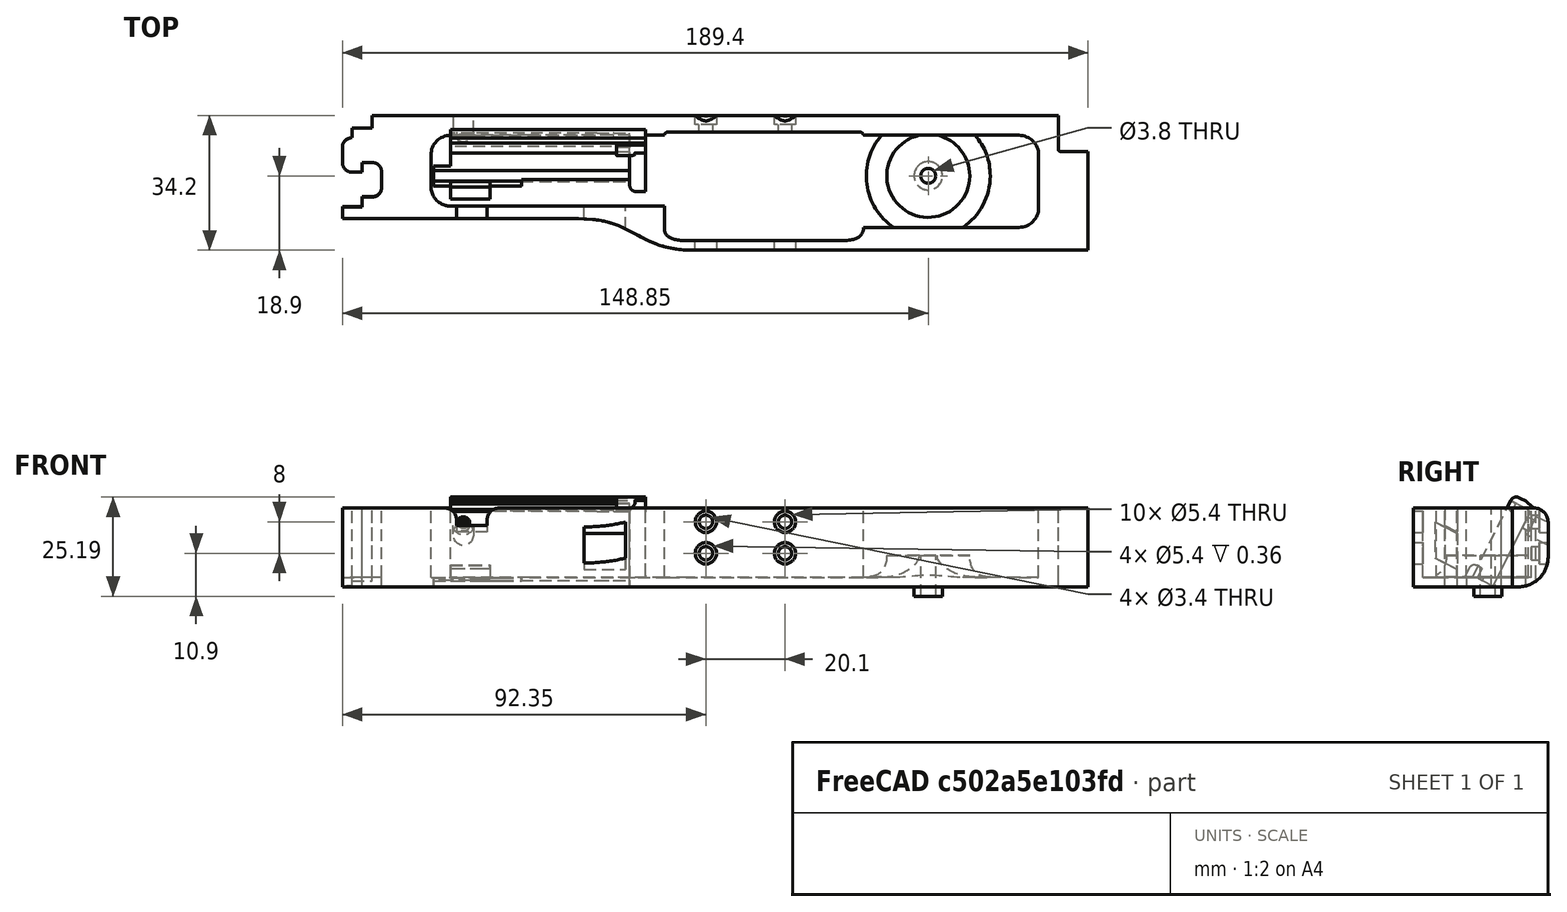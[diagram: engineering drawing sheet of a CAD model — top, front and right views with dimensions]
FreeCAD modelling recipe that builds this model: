
FCSTD DOCUMENT  (FreeCAD 0.19R0.19.2)
Label: v0_99
License: All rights reserved
LicenseURL: http://en.wikipedia.org/wiki/All_rights_reserved
objects: Sketcher::SketchObject×34, Part::Extrusion×28, Part::Cut×14, Part::Fillet×13, Part::MultiFuse×10, Part::Box×8, App::MeasureDistance×4, Part::Revolution×1, Mesh::Feature×1
note: 108 computed .brp shape members not serialized (recipe doc carries the construction recipe); baked Part::Feature solids carry a one-line shape summary decoded from their .brp

FEATURE [Sketcher::SketchObject] Sketch
  FullyConstrained = true
  sketch-geometry (36):
    g0: LineSegment StartX=0 StartY=0 StartZ=0 EndX=154.4 EndY=0 EndZ=0
    g1: LineSegment StartX=154.4 StartY=0 StartZ=0 EndX=154.4 EndY=-7.6 EndZ=0
    g2: LineSegment StartX=32.5209 StartY=-26.2 StartZ=0 EndX=-7.5 EndY=-26.2 EndZ=0
    g3: LineSegment StartX=61.85 StartY=-34.2 StartZ=0 EndX=161.9 EndY=-34.2 EndZ=0
    g4-g8: Circle x5 (B-spline internal-alignment scaffolding for g9; pole/knot coordinates omitted)
    g9: BSplineCurve PolesCount=5 KnotsCount=3 Degree=3 IsPeriodic=0
    g10: GeomPoint X=61.85 Y=-34.2 Z=0
    g11: GeomPoint X=47.185 Y=-30.2 Z=0
    g12: GeomPoint X=32.5209 Y=-26.2 Z=0
    g13: Circle CenterX=121.35 CenterY=-14.3 CenterZ=0 NormalX=0 NormalY=0 NormalZ=1 AngleXU=0 Radius=3.25
    g14: LineSegment StartX=-7.5 StartY=-26.2 StartZ=0 EndX=-27.5 EndY=-26.2 EndZ=0
    g15: LineSegment StartX=-20 StartY=0 StartZ=0 EndX=0 EndY=0 EndZ=0
    g16: LineSegment StartX=-25 StartY=-3.1 StartZ=0 EndX=-20 EndY=-3.1 EndZ=0
    g17: LineSegment StartX=-25 StartY=-3.1 StartZ=0 EndX=-25 EndY=-5.6 EndZ=0
    g18: LineSegment StartX=-27.5 StartY=-8.1 StartZ=0 EndX=-27.5 EndY=-11.85 EndZ=0
    g19: ArcOfCircle CenterX=-25 CenterY=-8.1 CenterZ=0 NormalX=0 NormalY=0 NormalZ=1 AngleXU=0 Radius=2.5 StartAngle=1.5708 EndAngle=3.14159
    g20: LineSegment StartX=-25 StartY=-14.35 StartZ=0 EndX=-22.5 EndY=-14.35 EndZ=0
    g21: ArcOfCircle CenterX=-25 CenterY=-11.85 CenterZ=0 NormalX=0 NormalY=0 NormalZ=1 AngleXU=0 Radius=2.5 StartAngle=3.14159 EndAngle=4.71239
    g22: LineSegment StartX=-22.5 StartY=-14.35 StartZ=0 EndX=-22.5 EndY=-11.85 EndZ=0
    g23: LineSegment StartX=-22.5 StartY=-11.85 StartZ=0 EndX=-20 EndY=-11.85 EndZ=0
    g24: ArcOfCircle CenterX=-20 CenterY=-14.35 CenterZ=0 NormalX=0 NormalY=0 NormalZ=1 AngleXU=0 Radius=2.5 StartAngle=8e-16 EndAngle=1.5708
    g25: LineSegment StartX=-17.5 StartY=-14.35 StartZ=0 EndX=-17.5 EndY=-18.1 EndZ=0
    g26: ArcOfCircle CenterX=-20 CenterY=-18.1 CenterZ=0 NormalX=0 NormalY=0 NormalZ=1 AngleXU=0 Radius=2.5 StartAngle=4.71239 EndAngle=6.28319
    g27: LineSegment StartX=-22.5 StartY=-20.6 StartZ=0 EndX=-20 EndY=-20.6 EndZ=0
    g28: LineSegment StartX=-22.5 StartY=-20.6 StartZ=0 EndX=-22.5 EndY=-23.1 EndZ=0
    g29: LineSegment StartX=-27.5 StartY=-23.1 StartZ=0 EndX=-22.5 EndY=-23.1 EndZ=0
    g30: LineSegment StartX=-20 StartY=-3.1 StartZ=0 EndX=-20 EndY=0 EndZ=0
    g31: LineSegment StartX=-27.5 StartY=-23.1 StartZ=0 EndX=-27.5 EndY=-26.2 EndZ=0
    g32: LineSegment StartX=154.4 StartY=-7.6 StartZ=0 EndX=154.4 EndY=-8.6 EndZ=0
    g33: ArcOfCircle CenterX=154.9 CenterY=-8.6 CenterZ=0 NormalX=0 NormalY=0 NormalZ=1 AngleXU=0 Radius=0.5 StartAngle=3.14159 EndAngle=4.71239
    g34: LineSegment StartX=154.9 StartY=-9.1 StartZ=0 EndX=161.9 EndY=-9.1 EndZ=0
    g35: LineSegment StartX=161.9 StartY=-34.2 StartZ=0 EndX=161.9 EndY=-9.1 EndZ=0
  constraints (72):
    c: PointOnObject(g0,g-2)
    c: Horizontal(g0)
    c: Distance(g0) = 154.4
    c: DistanceY(g-1,g0) = 0
    c: Vertical(g1)
    c: Distance(g1) = 7.6
    c: Coincident(g1,g0)
    c: Horizontal(g3)
    c: Horizontal(g2)
    c: Block(g2)
    c: Block(g3)
    c: Coincident(g9,g3)
    c: Weight(g4) = 1
    c: Equal(g4, g5-g8) x4
    c: Coincident(g9,g2)
    c: InternalAlignment(g4-g8 -> g9) x5
    c: InternalAlignment(g10,g9)
    c: InternalAlignment(g11,g9)
    c: InternalAlignment(g12,g9)
    c: Block(g9)
    c: Block(g13)
    c: Coincident(g14,g2)
    c: Horizontal(g14)
    c: Distance(g14) = 20
    c: Horizontal(g15)
    c: Distance(g15) = 20
    c: Coincident(g15,g0)
    c: Horizontal(g16)
    c: Vertical(g17)
    c: Coincident(g17,g16)
    c: Vertical(g18)
    c: Coincident(g19,g17)
    c: Block(g19)
    c: Coincident(g18,g19)
    c: Horizontal(g20)
    c: Coincident(g21,g18)
    c: Block(g21)
    c: Block(g20)
    c: Vertical(g22)
    c: Coincident(g22,g20)
    c: Horizontal(g23)
    c: Coincident(g23,g22)
    c: Coincident(g24,g23)
    c: Vertical(g25)
    c: Block(g24)
    c: Coincident(g25,g24)
    c: Coincident(g26,g25)
    c: Block(g26)
    c: Horizontal(g27)
    c: Coincident(g27,g26)
    c: Vertical(g28)
    c: Coincident(g28,g27)
    c: Horizontal(g29)
    c: Coincident(g29,g28)
    c: Block(g16)
    c: Block(g29)
    c: Coincident(g30,g16)
    c: Coincident(g30,g15)
    c: Vertical(g30)
    c: Coincident(g31,g29)
    c: Coincident(g31,g14)
    c: Vertical(g31)
    c: Vertical(g32)
    c: Distance(g32) = 1
    c: Coincident(g32,g1)
    c: Coincident(g33,g32)
    c: Block(g33)
    c: Coincident(g34,g33)
    c: Horizontal(g34)
    c: Coincident(g35,g3)
    c: Vertical(g35)
    c: Coincident(g34,g35)
FEATURE [Part::Extrusion] Extrude  label="mainBodyBaseExtrude"
  Base = -> Sketch
  Dir = (0,0,1)
  DirMode = 2
  FaceMakerClass = Part::FaceMakerBullseye
  LengthFwd = 2.4
  LengthRev = 0
  Solid = true
  Symmetric = false
FEATURE [Sketcher::SketchObject] Sketch001
  FullyConstrained = true
  sketch-geometry (59):
    g0: ArcOfCircle CenterX=144.4 CenterY=-10 CenterZ=0 NormalX=0 NormalY=0 NormalZ=1 AngleXU=0 Radius=5 StartAngle=4.345e-13 EndAngle=1.5708
    g1: LineSegment StartX=32.5209 StartY=-26.2 StartZ=0 EndX=-7.49911 EndY=-26.2 EndZ=0
    g2: LineSegment StartX=61.85 StartY=-34.2 StartZ=0 EndX=161.9 EndY=-34.2 EndZ=0
    g3: LineSegment StartX=0 StartY=0 StartZ=0 EndX=154.4 EndY=0 EndZ=0
    g4-g8: Circle x5 (B-spline internal-alignment scaffolding for g9; pole/knot coordinates omitted)
    g9: BSplineCurve PolesCount=5 KnotsCount=3 Degree=3 IsPeriodic=0
    g10: GeomPoint X=61.85 Y=-34.2 Z=0
    g11: GeomPoint X=47.1857 Y=-30.2 Z=0
    g12: GeomPoint X=32.5209 Y=-26.2 Z=0
    g13: LineSegment StartX=154.4 StartY=0 StartZ=0 EndX=154.4 EndY=-7.6 EndZ=0
    g14: LineSegment StartX=20 StartY=-5 StartZ=0 EndX=54.35 EndY=-5 EndZ=0
    g15: LineSegment StartX=104.85 StartY=-5 StartZ=0 EndX=144.4 EndY=-5 EndZ=0
    g16: LineSegment StartX=54.35 StartY=-23 StartZ=0 EndX=20 EndY=-23 EndZ=0
    g17: LineSegment StartX=-27.4991 StartY=-26.2 StartZ=0 EndX=-7.49911 EndY=-26.2 EndZ=0
    g18: LineSegment StartX=-20 StartY=0 StartZ=0 EndX=0 EndY=0 EndZ=0
    g19: LineSegment StartX=-27.4991 StartY=-23.2 StartZ=0 EndX=-22.5 EndY=-23.2 EndZ=0
    g20: LineSegment StartX=-22.5 StartY=-20.7 StartZ=0 EndX=-22.5 EndY=-23.2 EndZ=0
    g21: LineSegment StartX=-22.5 StartY=-20.7 StartZ=0 EndX=-20 EndY=-20.7 EndZ=0
    g22: ArcOfCircle CenterX=-20 CenterY=-18.2 CenterZ=0 NormalX=0 NormalY=0 NormalZ=1 AngleXU=0 Radius=2.5 StartAngle=4.71239 EndAngle=6.28319
    g23: LineSegment StartX=-17.5 StartY=-14.4 StartZ=0 EndX=-17.5 EndY=-18.2 EndZ=0
    g24: ArcOfCircle CenterX=-20 CenterY=-14.4 CenterZ=0 NormalX=0 NormalY=0 NormalZ=1 AngleXU=0 Radius=2.5 StartAngle=9e-16 EndAngle=1.5708
    g25: LineSegment StartX=-22.5 StartY=-11.9 StartZ=0 EndX=-20 EndY=-11.9 EndZ=0
    g26: LineSegment StartX=-22.5 StartY=-14.4 StartZ=0 EndX=-22.5 EndY=-11.9 EndZ=0
    g27: LineSegment StartX=-25 StartY=-14.4 StartZ=0 EndX=-22.5 EndY=-14.4 EndZ=0
    g28: ArcOfCircle CenterX=-25 CenterY=-11.9 CenterZ=0 NormalX=0 NormalY=0 NormalZ=1 AngleXU=0 Radius=2.5 StartAngle=3.14159 EndAngle=4.71239
    g29: LineSegment StartX=-27.5 StartY=-8.1 StartZ=0 EndX=-27.5 EndY=-11.9 EndZ=0
    g30: ArcOfCircle CenterX=-25 CenterY=-8.1 CenterZ=0 NormalX=0 NormalY=0 NormalZ=1 AngleXU=0 Radius=2.5 StartAngle=1.5708 EndAngle=3.14159
    g31: LineSegment StartX=-25 StartY=-3.1 StartZ=0 EndX=-25 EndY=-5.6 EndZ=0
    g32: LineSegment StartX=-20 StartY=-3.1 StartZ=0 EndX=-25 EndY=-3.1 EndZ=0
    g33: LineSegment StartX=-20 StartY=0 StartZ=0 EndX=-20 EndY=-3.1 EndZ=0
    g34: LineSegment StartX=-27.4991 StartY=-26.2 StartZ=0 EndX=-27.4991 EndY=-23.2 EndZ=0
    g35: LineSegment StartX=4.09e-14 StartY=-5 StartZ=0 EndX=20 EndY=-5 EndZ=0
    g36: ArcOfCircle CenterX=7.1e-15 CenterY=-18 CenterZ=0 NormalX=0 NormalY=0 NormalZ=1 AngleXU=0 Radius=5 StartAngle=3.14159 EndAngle=4.71239
    g37: ArcOfCircle CenterX=4.26e-14 CenterY=-10 CenterZ=0 NormalX=0 NormalY=0 NormalZ=1 AngleXU=0 Radius=5 StartAngle=1.5708 EndAngle=3.14159
    g38: LineSegment StartX=-5 StartY=-18 StartZ=0 EndX=-5 EndY=-10 EndZ=0
    g39: LineSegment StartX=6.2e-15 StartY=-23 StartZ=0 EndX=20 EndY=-23 EndZ=0
    g40: LineSegment StartX=154.4 StartY=-7.6 StartZ=0 EndX=154.4 EndY=-8.6 EndZ=0
    g41: LineSegment StartX=154.9 StartY=-9.1 StartZ=0 EndX=161.9 EndY=-9.1 EndZ=0
    g42: LineSegment StartX=161.9 StartY=-34.2 StartZ=0 EndX=161.9 EndY=-9.1 EndZ=0
    g43: ArcOfCircle CenterX=154.9 CenterY=-8.6 CenterZ=0 NormalX=0 NormalY=0 NormalZ=1 AngleXU=0 Radius=0.5 StartAngle=3.14159 EndAngle=4.71299
    g44: LineSegment StartX=104.85 StartY=-28.3916 StartZ=0 EndX=144.408 EndY=-28.3916 EndZ=0
    g45: LineSegment StartX=149.4 StartY=-10 StartZ=0 EndX=149.4 EndY=-23.4 EndZ=0
    g46: ArcOfCircle CenterX=144.408 CenterY=-23.4 CenterZ=0 NormalX=0 NormalY=0 NormalZ=1 AngleXU=0 Radius=4.99164 StartAngle=4.71239 EndAngle=6.28319
    g47: LineSegment StartX=104.05 StartY=-4.2 StartZ=0 EndX=55.15 EndY=-4.2 EndZ=0
    g48: ArcOfCircle CenterX=104.05 CenterY=-5 CenterZ=0 NormalX=0 NormalY=0 NormalZ=1 AngleXU=0 Radius=0.8 StartAngle=0 EndAngle=1.5708
    g49: ArcOfCircle CenterX=55.15 CenterY=-5 CenterZ=0 NormalX=0 NormalY=0 NormalZ=1 AngleXU=0 Radius=0.8 StartAngle=1.57079 EndAngle=3.14159
    g50: BSplineCurve PolesCount=3 KnotsCount=2 Degree=2 IsPeriodic=0
    g51: GeomPoint X=54.35 Y=-28.7916 Z=0
    g52: GeomPoint X=60.35 Y=-31.7916 Z=0
    g53: BSplineCurve PolesCount=3 KnotsCount=2 Degree=2 IsPeriodic=0
    g54: GeomPoint X=98.85 Y=-31.7916 Z=0
    g55: GeomPoint X=104.85 Y=-28.7833 Z=0
    g56: LineSegment StartX=104.85 StartY=-28.3916 StartZ=0 EndX=104.85 EndY=-28.7833 EndZ=0
    g57: LineSegment StartX=54.35 StartY=-28.7916 StartZ=0 EndX=54.35 EndY=-23 EndZ=0
    g58: LineSegment StartX=60.35 StartY=-31.7916 StartZ=0 EndX=98.85 EndY=-31.7916 EndZ=0
  constraints (127):
    c: PointOnObject(g3,g-2)
    c: DistanceY(g-1,g3) = 0
    c: Block(g0)
    c: Horizontal(g2)
    c: Horizontal(g1)
    c: Distance(g1) = 40.02
    c: Horizontal(g3)
    c: Block(g2)
    c: Block(g3)
    c: Coincident(g9,g2)
    c: Weight(g4) = 1
    c: Equal(g4, g5-g8) x4
    c: Coincident(g9,g1)
    c: InternalAlignment(g4-g8 -> g9) x5
    c: InternalAlignment(g10,g9)
    c: InternalAlignment(g11,g9)
    c: InternalAlignment(g12,g9)
    c: Block(g9)
    c: Vertical(g13)
    c: Coincident(g13,g3)
    c: Distance(g13) = 7.6
    c: Block(g13)
    c: Horizontal(g14)
    c: Coincident(g15,g0)
    c: Horizontal(g15)
    c: Horizontal(g16)
    c: Horizontal(g17)
    c: Distance(g17) = 20
    c: Coincident(g1,g17)
    c: Horizontal(g18)
    c: Distance(g18) = 20
    c: Coincident(g18,g3)
    c: Horizontal(g32)
    c: Vertical(g31)
    c: Coincident(g30,g31)
    c: Vertical(g29)
    c: Block(g30)
    c: Coincident(g28,g29)
    c: Block(g28)
    c: Horizontal(g27)
    c: Coincident(g27,g28)
    c: Vertical(g26)
    c: Coincident(g26,g27)
    c: Horizontal(g25)
    c: Coincident(g24,g25)
    c: Block(g24)
    c: Vertical(g23)
    c: Coincident(g22,g23)
    c: Block(g22)
    c: Horizontal(g21)
    c: Coincident(g21,g22)
    c: Vertical(g20)
    c: Coincident(g20,g21)
    c: Horizontal(g19)
    c: Coincident(g19,g20)
    c: Coincident(g33,g18)
    c: Coincident(g33,g32)
    c: Vertical(g33)
    c: Coincident(g34,g17)
    c: Coincident(g34,g19)
    c: Vertical(g34)
    c: Block(g34)
    c: Block(g19)
    c: Block(g23)
    c: Block(g27)
    c: Block(g26)
    c: Block(g25)
    c: Block(g29)
    c: Block(g32)
    c: Block(g31)
    c: Horizontal(g35)
    c: Distance(g35) = 20
    c: Block(g36)
    c: Block(g37)
    c: Coincident(g38,g36)
    c: Coincident(g38,g37)
    c: Vertical(g38)
    c: Coincident(g39,g36)
    c: Coincident(g39,g16)
    c: Horizontal(g39)
    c: Block(g39)
    c: Block(g35)
    c: Block(g14)
    c: Vertical(g40)
    c: Distance(g40) = 1
    c: Coincident(g40,g13)
    c: Horizontal(g41)
    c: Coincident(g42,g2)
    c: Vertical(g42)
    c: Coincident(g42,g41)
    c: Distance(g42) = 25.1
    c: Coincident(g43,g40)
    c: Coincident(g43,g41)
    c: Block(g40)
    c: Block(g43)
    c: Horizontal(g44)
    c: Vertical(g45)
    c: Distance(g45) = 13.4
    c: Coincident(g45,g0)
    c: Block(g44)
    c: Block(g45)
    c: Coincident(g46,g45)
    c: Coincident(g46,g44)
    c: Block(g46)
    c: Horizontal(g47)
    c: Coincident(g48,g15)
    c: Coincident(g48,g47)
    c: Block(g48)
    c: Coincident(g49,g14)
    c: Coincident(g49,g47)
    c: Block(g49)
    c: Distance(g16) = 34.35
    c: InternalAlignment(g51,g50)
    c: InternalAlignment(g52,g50)
    c: Block(g50)
    c: InternalAlignment(g54,g53)
    c: InternalAlignment(g55,g53)
    c: Block(g53)
    c: Coincident(g56,g44)
    c: Coincident(g56,g53)
    c: Vertical(g56)
    c: Coincident(g57,g50)
    c: Coincident(g57,g16)
    c: Vertical(g57)
    c: Coincident(g58,g50)
    c: Coincident(g58,g53)
    c: Horizontal(g58)
FEATURE [Sketcher::SketchObject] Sketch005
  FullyConstrained = true
  Placement = pos=(0,0,0) rot=(1,0,0;1.5708rad)
  sketch-geometry (4):
    g0: Circle CenterX=84.95 CenterY=16.5 CenterZ=0 NormalX=0 NormalY=0 NormalZ=1 AngleXU=0 Radius=1.7
    g1: Circle CenterX=84.95 CenterY=8.5 CenterZ=0 NormalX=0 NormalY=0 NormalZ=1 AngleXU=0 Radius=1.7
    g2: Circle CenterX=64.85 CenterY=8.5 CenterZ=0 NormalX=0 NormalY=0 NormalZ=1 AngleXU=0 Radius=1.7
    g3: Circle CenterX=64.85 CenterY=16.5 CenterZ=0 NormalX=0 NormalY=0 NormalZ=1 AngleXU=0 Radius=1.7
  constraints (4):
    c: Block(g0)
    c: Block(g1)
    c: Block(g2)
    c: Block(g3)
FEATURE [Part::Extrusion] Extrude004  label="removeFromMainBodyToCreateScrewHolesForSolenoidExtrude004"
  Base = -> Sketch005
  Dir = (0,-1,1.1e-15)
  DirMode = 2
  FaceMakerClass = Part::FaceMakerBullseye
  LengthFwd = 10
  LengthRev = 0
  Solid = true
  Symmetric = false
FEATURE [Sketcher::SketchObject] Sketch004
  FullyConstrained = true
  Placement = pos=(0,0,0) rot=(1,0,0;1.5708rad)
  sketch-geometry (12):
    g0: LineSegment StartX=15.75 StartY=2.5 StartZ=0 EndX=15.75 EndY=0 EndZ=0
    g1: Circle CenterX=15.75 CenterY=2.5 CenterZ=0 NormalX=0 NormalY=0 NormalZ=1 AngleXU=0 Radius=1
    g2: Circle CenterX=10.55 CenterY=2.5 CenterZ=0 NormalX=0 NormalY=0 NormalZ=1 AngleXU=0 Radius=1
    g3: Circle CenterX=10.55 CenterY=8 CenterZ=0 NormalX=0 NormalY=0 NormalZ=1 AngleXU=0 Radius=1
    g4: BSplineCurve PolesCount=3 KnotsCount=2 Degree=2 IsPeriodic=0
    g5: GeomPoint X=15.75 Y=2.5 Z=0
    g6: GeomPoint X=10.55 Y=8 Z=0
    g7: LineSegment StartX=1.9 StartY=8 StartZ=0 EndX=10.55 EndY=8 EndZ=0
    g8: LineSegment StartX=1.9 StartY=-2.4 StartZ=0 EndX=1.9 EndY=8 EndZ=0
    g9: LineSegment StartX=3.30092 StartY=-2.4 StartZ=0 EndX=3.30092 EndY=0 EndZ=0
    g10: LineSegment StartX=15.75 StartY=0 StartZ=0 EndX=3.30092 EndY=0 EndZ=0
    g11: LineSegment StartX=3.30092 StartY=-2.4 StartZ=0 EndX=1.9 EndY=-2.4 EndZ=0
  constraints (26):
    c: Vertical(g0)
    c: Distance(g0) = 2.5
    c: Coincident(g4,g0)
    c: Weight(g1) = 1
    c: Equal(g1,g2)
    c: Equal(g1,g3)
    c: InternalAlignment(g1,g4)
    c: InternalAlignment(g2,g4)
    c: InternalAlignment(g3,g4)
    c: InternalAlignment(g5,g4)
    c: InternalAlignment(g6,g4)
    c: Block(g4)
    c: Coincident(g7,g4)
    c: Horizontal(g7)
    c: Vertical(g8)
    c: Coincident(g8,g7)
    c: Block(g8)
    c: Vertical(g9)
    c: Coincident(g10,g0)
    c: PointOnObject(g10,g-1)
    c: Horizontal(g10)
    c: Coincident(g10,g9)
    c: Block(g9)
    c: Coincident(g11,g9)
    c: Coincident(g11,g8)
    c: Horizontal(g11)
FEATURE [Sketcher::SketchObject] Sketch007
  FullyConstrained = true
  Placement = pos=(0,-14.3,2.37) rot=(-1,0,0;2.03453rad)
  sketch-geometry (6):
    g0: LineSegment StartX=0 StartY=0 StartZ=0 EndX=45.5 EndY=0 EndZ=0
    g1: LineSegment StartX=0 StartY=0 StartZ=0 EndX=0 EndY=-21.2 EndZ=0
    g2: LineSegment StartX=45.5 StartY=0 StartZ=0 EndX=49.5 EndY=0 EndZ=0
    g3: LineSegment StartX=49.5 StartY=0 StartZ=0 EndX=49.5 EndY=-21.2 EndZ=0
    g4: LineSegment StartX=49.5 StartY=-21.2 StartZ=0 EndX=0 EndY=-21.2 EndZ=0
    g5: Circle CenterX=3.25 CenterY=-18.05 CenterZ=0 NormalX=0 NormalY=0 NormalZ=1 AngleXU=0 Radius=1.6
  constraints (15):
    c: Coincident(g0,g-1)
    c: Horizontal(g0)
    c: Distance(g0) = 45.5
    c: Coincident(g1,g0)
    c: Vertical(g1)
    c: Horizontal(g2)
    c: Distance(g2) = 4
    c: Coincident(g2,g0)
    c: Coincident(g3,g2)
    c: Vertical(g3)
    c: Block(g3)
    c: Coincident(g4,g3)
    c: Horizontal(g4)
    c: Coincident(g4,g1)
    c: Block(g5)
FEATURE [Part::Extrusion] Extrude005  label="solenoidDriverHolderExtrude005"
  Base = -> Sketch007
  Dir = (0,0.894389,-0.447291)
  DirMode = 2
  FaceMakerClass = Part::FaceMakerBullseye
  LengthFwd = 10
  LengthRev = 0
  Placement = pos=(0,0,-2) rot=(0,0,1;0rad)
  Solid = true
  Symmetric = false
FEATURE [Sketcher::SketchObject] Sketch008
  FullyConstrained = false
  Placement = pos=(0,-4.3,-2.6) rot=(-1,0,0;2.03453rad)
  sketch-geometry (1):
    g0: Circle CenterX=42.25 CenterY=-3.15 CenterZ=0 NormalX=0 NormalY=0 NormalZ=1 AngleXU=0 Radius=4.5
FEATURE [Sketcher::SketchObject] Sketch009
  FullyConstrained = true
  Placement = pos=(0,-4.3,-2.6) rot=(-1,0,0;2.03453rad)
  sketch-geometry (1):
    g0: Circle CenterX=3.25 CenterY=-18.0217 CenterZ=0 NormalX=0 NormalY=0 NormalZ=1 AngleXU=0 Radius=2.6
  constraints (1):
    c: Block(g0)
FEATURE [Sketcher::SketchObject] Sketch010
  FullyConstrained = true
  Placement = pos=(0,-14.3,2.37) rot=(-1,0,0;2.03453rad)
  sketch-geometry (1):
    g0: Circle CenterX=3.25 CenterY=-18.05 CenterZ=0 NormalX=0 NormalY=0 NormalZ=1 AngleXU=0 Radius=1.6
  constraints (1):
    c: Block(g0)
FEATURE [Part::Extrusion] Extrude008  label="removeFromScrewHole3"
  Base = -> Sketch010
  Dir = (0,0.894389,-0.447291)
  DirMode = 2
  FaceMakerClass = Part::FaceMakerBullseye
  LengthFwd = -25
  LengthRev = 0
  Placement = pos=(0,4,-4) rot=(0,0,1;0rad)
  Solid = true
  Symmetric = false
FEATURE [Sketcher::SketchObject] Sketch011
  FullyConstrained = true
  Placement = pos=(0,-14.3,2.37) rot=(-1,0,0;2.03453rad)
  sketch-geometry (4):
    g0: LineSegment StartX=49.5 StartY=-21.2 StartZ=0 EndX=49.5 EndY=-22.8 EndZ=0
    g1: LineSegment StartX=49.5 StartY=-22.8 StartZ=0 EndX=0.002238 EndY=-22.8 EndZ=0
    g2: LineSegment StartX=0.002238 StartY=-21.2 StartZ=0 EndX=0.002238 EndY=-22.8 EndZ=0
    g3: LineSegment StartX=49.5 StartY=-21.2 StartZ=0 EndX=0.002238 EndY=-21.2 EndZ=0
  constraints (10):
    c: Vertical(g0)
    c: Distance(g0) = 1.6
    c: Coincident(g1,g0)
    c: Horizontal(g1)
    c: Vertical(g2)
    c: Coincident(g2,g1)
    c: Coincident(g3,g0)
    c: Coincident(g3,g2)
    c: Horizontal(g3)
    c: Block(g3)
FEATURE [Part::Extrusion] Extrude009  label="solenoidDriverTopLipFront"
  Base = -> Sketch011
  Dir = (0,0.894389,-0.447291)
  DirMode = 2
  FaceMakerClass = Part::FaceMakerBullseye
  LengthFwd = -2
  LengthRev = 0
  Placement = pos=(0,-2.9,-0.35) rot=(0,0,1;0rad)
  Solid = true
  Symmetric = false
FEATURE [Sketcher::SketchObject] Sketch012
  FullyConstrained = true
  Placement = pos=(0,-14.3,2.37) rot=(-1,0,0;2.03453rad)
  sketch-geometry (4):
    g0: LineSegment StartX=49.5 StartY=-21.2 StartZ=0 EndX=49.5 EndY=-22.8 EndZ=0
    g1: LineSegment StartX=49.5 StartY=-22.8 StartZ=0 EndX=0.002238 EndY=-22.8 EndZ=0
    g2: LineSegment StartX=0.002238 StartY=-21.2 StartZ=0 EndX=0.002238 EndY=-22.8 EndZ=0
    g3: LineSegment StartX=49.5 StartY=-21.2 StartZ=0 EndX=0.002238 EndY=-21.2 EndZ=0
  constraints (10):
    c: Vertical(g0)
    c: Distance(g0) = 1.6
    c: Coincident(g1,g0)
    c: Horizontal(g1)
    c: Vertical(g2)
    c: Coincident(g2,g1)
    c: Coincident(g3,g0)
    c: Coincident(g3,g2)
    c: Horizontal(g3)
    c: Block(g3)
FEATURE [Part::Extrusion] Extrude010  label="solenoidDriverTopLipLowerExtrude010"
  Base = -> Sketch012
  Dir = (0,0.894389,-0.447291)
  DirMode = 2
  FaceMakerClass = Part::FaceMakerBullseye
  LengthFwd = 5.05
  LengthRev = 0
  Solid = true
  Symmetric = false
FEATURE [Sketcher::SketchObject] Sketch015
  FullyConstrained = true
  Placement = pos=(0,-14.3,2.37) rot=(-1,0,0;2.03453rad)
  sketch-geometry (4):
    g0: LineSegment StartX=0 StartY=1.5 StartZ=0 EndX=0 EndY=0 EndZ=0
    g1: LineSegment StartX=0 StartY=1.5 StartZ=0 EndX=5 EndY=1.5 EndZ=0
    g2: LineSegment StartX=5 StartY=1.5 StartZ=0 EndX=5 EndY=0 EndZ=0
    g3: LineSegment StartX=0 StartY=0 StartZ=0 EndX=5 EndY=0 EndZ=0
  constraints (13):
    c: Vertical(g0)
    c: Distance(g0) = 1.5
    c: Horizontal(g1)
    c: Distance(g1) = 5
    c: Coincident(g1,g0)
    c: Vertical(g2)
    c: Distance(g2) = 1.5
    c: Coincident(g2,g1)
    c: Block(g1)
    c: Block(g2)
    c: Block(g0)
    c: Coincident(g3,g0)
    c: Coincident(g3,g2)
FEATURE [Part::Extrusion] Extrude013  label="solenoidDriverBottomLipTopExtrude012"
  Base = -> Sketch015
  Dir = (0,0.894389,-0.447291)
  DirMode = 2
  FaceMakerClass = Part::FaceMakerBullseye
  LengthFwd = -6.5
  LengthRev = 0
  Placement = pos=(0,-14.15,19.65) rot=(1,0,0;1.5708rad)
  Solid = true
  Symmetric = false
FEATURE [Sketcher::SketchObject] Sketch016
  FullyConstrained = true
  Placement = pos=(0,0,0) rot=(1,0,0;1.5708rad)
  sketch-geometry (4):
    g0: Circle CenterX=84.15 CenterY=16.5 CenterZ=0 NormalX=0 NormalY=0 NormalZ=1 AngleXU=0 Radius=2.7
    g1: Circle CenterX=64.05 CenterY=16.5 CenterZ=0 NormalX=0 NormalY=0 NormalZ=1 AngleXU=0 Radius=2.7
    g2: Circle CenterX=64.05 CenterY=8.5 CenterZ=0 NormalX=0 NormalY=0 NormalZ=1 AngleXU=0 Radius=2.7
    g3: Circle CenterX=84.15 CenterY=8.5 CenterZ=0 NormalX=0 NormalY=0 NormalZ=1 AngleXU=0 Radius=2.7
  constraints (4):
    c: Block(g0)
    c: Block(g1)
    c: Block(g3)
    c: Block(g2)
FEATURE [Part::Extrusion] Extrude014  label="removeFromMainBodyToCreateScrewHoleCounterSinks"
  Base = -> Sketch016
  Dir = (0,-1,1.1e-15)
  DirMode = 2
  FaceMakerClass = Part::FaceMakerBullseye
  LengthFwd = 1.9
  LengthRev = 0
  Placement = pos=(0.8,-0.36,0) rot=(0,0,1;0rad)
  Solid = true
  Symmetric = false
FEATURE [Part::Extrusion] Extrude015  label="removeFromScrewHole2Extrude007"
  Base = -> Sketch009
  Dir = (0,0.894389,-0.447291)
  DirMode = 2
  FaceMakerClass = Part::FaceMakerBullseye
  LengthFwd = 10
  LengthRev = 0
  Placement = pos=(0,-8,2) rot=(0,0,1;0rad)
  Solid = true
  Symmetric = false
FEATURE [Sketcher::SketchObject] Sketch017
  FullyConstrained = true
  Placement = pos=(0,-14.3,2.37) rot=(-1,0,0;2.03453rad)
  sketch-geometry (4):
    g0: LineSegment StartX=0 StartY=1.5 StartZ=0 EndX=0 EndY=0 EndZ=0
    g1: LineSegment StartX=0 StartY=1.5 StartZ=0 EndX=5 EndY=1.5 EndZ=0
    g2: LineSegment StartX=5 StartY=1.5 StartZ=0 EndX=5 EndY=0 EndZ=0
    g3: LineSegment StartX=0 StartY=0 StartZ=0 EndX=5 EndY=0 EndZ=0
  constraints (13):
    c: Vertical(g0)
    c: Distance(g0) = 1.5
    c: Horizontal(g1)
    c: Distance(g1) = 5
    c: Coincident(g1,g0)
    c: Vertical(g2)
    c: Distance(g2) = 1.5
    c: Coincident(g2,g1)
    c: Block(g1)
    c: Block(g2)
    c: Block(g0)
    c: Coincident(g3,g0)
    c: Coincident(g3,g2)
FEATURE [Part::Extrusion] Extrude016  label="solenoidDriverBottomLipTopExtrude013"
  Base = -> Sketch017
  Dir = (0,0.894389,-0.447291)
  DirMode = 2
  FaceMakerClass = Part::FaceMakerBullseye
  LengthFwd = -6.5
  LengthRev = 0
  Placement = pos=(0,-15.45,20.3) rot=(1,0,0;1.5708rad)
  Solid = true
  Symmetric = false
FEATURE [Part::Fillet] Fillet005  label="solenoidDriverBottomLipTopFillet005"
  Base = -> Extrude016
  Edges = 1 edges r=1.4: [Edge6]
FEATURE [Sketcher::SketchObject] Sketch018
  FullyConstrained = true
  Placement = pos=(38.5,-14.3,2.37) rot=(-1,0,0;2.03453rad)
  sketch-geometry (4):
    g0: LineSegment StartX=11 StartY=0 StartZ=0 EndX=11 EndY=1.5 EndZ=0
    g1: LineSegment StartX=11 StartY=0 StartZ=0 EndX=3.6 EndY=0 EndZ=0
    g2: LineSegment StartX=3.6 StartY=0 StartZ=0 EndX=3.6 EndY=1.5 EndZ=0
    g3: LineSegment StartX=11 StartY=1.5 StartZ=0 EndX=3.6 EndY=1.5 EndZ=0
  constraints (12):
    c: PointOnObject(g0,g-1)
    c: Vertical(g0)
    c: Distance(g0) = 1.5
    c: Horizontal(g1)
    c: Distance(g1) = 7.4
    c: Coincident(g1,g0)
    c: Block(g0)
    c: Coincident(g2,g1)
    c: Vertical(g2)
    c: Coincident(g3,g0)
    c: Horizontal(g3)
    c: Coincident(g2,g3)
FEATURE [Part::Extrusion] Extrude017
  Base = -> Sketch018
  Dir = (0,0.894389,-0.447291)
  DirMode = 2
  FaceMakerClass = Part::FaceMakerBullseye
  LengthFwd = 4
  LengthRev = 0
  Placement = pos=(0,-8.212,34.025) rot=(1,0,0;1.5708rad)
  Solid = true
  Symmetric = false
FEATURE [Sketcher::SketchObject] Sketch019
  FullyConstrained = true
  Placement = pos=(0,0,0) rot=(1,0,0;1.5708rad)
  sketch-geometry (4):
    g0: Circle CenterX=84.95 CenterY=8.5 CenterZ=0 NormalX=0 NormalY=0 NormalZ=1 AngleXU=0 Radius=2.7
    g1: Circle CenterX=64.85 CenterY=8.5 CenterZ=0 NormalX=0 NormalY=0 NormalZ=1 AngleXU=0 Radius=2.7
    g2: Circle CenterX=64.85 CenterY=16.5 CenterZ=0 NormalX=0 NormalY=0 NormalZ=1 AngleXU=0 Radius=2.7
    g3: Circle CenterX=84.95 CenterY=16.5 CenterZ=0 NormalX=0 NormalY=0 NormalZ=1 AngleXU=0 Radius=2.7
  constraints (4):
    c: Block(g3)
    c: Block(g2)
    c: Block(g0)
    c: Block(g1)
FEATURE [Part::Extrusion] Extrude019  label="removeSolenoidAdjusterHoles"
  Base = -> Sketch019
  Dir = (0,-1,1.1e-15)
  DirMode = 2
  FaceMakerClass = Part::FaceMakerBullseye
  LengthFwd = 6
  LengthRev = 0
  Placement = pos=(0,-30,0) rot=(0,0,1;0rad)
  Solid = true
  Symmetric = false
FEATURE [Sketcher::SketchObject] Sketch020
  FullyConstrained = true
  Placement = pos=(0,-14.3,2.37) rot=(-1,0,0;2.03453rad)
  sketch-geometry (6):
    g0: LineSegment StartX=45.5 StartY=-21.2 StartZ=0 EndX=49.5 EndY=-21.2 EndZ=0
    g1: LineSegment StartX=45.5 StartY=0 StartZ=0 EndX=49.5 EndY=0 EndZ=0
    g2: LineSegment StartX=49.5 StartY=0 StartZ=0 EndX=49.5 EndY=-21.2 EndZ=0
    g3: LineSegment StartX=4 StartY=0 StartZ=0 EndX=4 EndY=-21.2 EndZ=0
    g4: LineSegment StartX=45.5 StartY=-21.2 StartZ=0 EndX=4 EndY=-21.2 EndZ=0
    g5: LineSegment StartX=4 StartY=0 StartZ=0 EndX=45.5 EndY=0 EndZ=0
  constraints (16):
    c: Horizontal(g0)
    c: Distance(g0) = 4
    c: Horizontal(g1)
    c: Distance(g1) = 4
    c: Coincident(g2,g1)
    c: Coincident(g2,g0)
    c: Vertical(g2)
    c: Block(g2)
    c: Vertical(g3)
    c: Coincident(g4,g0)
    c: Horizontal(g4)
    c: Coincident(g4,g3)
    c: Coincident(g5,g1)
    c: Horizontal(g5)
    c: Block(g3)
    c: Block(g5)
FEATURE [Part::Box] Box  label="Cube"
  AttacherType = Attacher::AttachEngine3D
  Height = 10
  Length = 190
  Placement = pos=(-30,0,0) rot=(0,0,1;0rad)
  Width = 10
FEATURE [Part::Fillet] Fillet008
  Base = -> Box
  Edges = 1 edges r=7.5: [Edge11]
FEATURE [Part::Box] Box001  label="Cube001"
  AttacherType = Attacher::AttachEngine3D
  Height = 10
  Length = 190
  Placement = pos=(-35,0,0) rot=(0,0,1;0rad)
  Width = 10
FEATURE [Part::Cut] Cut  label="filletMain"
  Base = -> Box001
  Placement = pos=(0,-10,0) rot=(0,0,1;0rad)
  Tool = -> Fillet008
FEATURE [Part::Box] Box002  label="Cube002"
  AttacherType = Attacher::AttachEngine3D
  Height = 30
  Length = 190
  Placement = pos=(-20,0,0) rot=(0,0,1;0rad)
  Width = 10
FEATURE [Part::Box] Box003  label="Cube003"
  AttacherType = Attacher::AttachEngine3D
  Height = 10
  Length = 190
  Placement = pos=(-90,-50,-10) rot=(0,0,1;0rad)
  Width = 50
FEATURE [Sketcher::SketchObject] Sketch021
  FullyConstrained = true
  Placement = pos=(0,-14.3,2.37) rot=(-1,0,0;2.03453rad)
  sketch-geometry (6):
    g0: LineSegment StartX=41.65 StartY=-3.15 StartZ=0 EndX=38.95 EndY=-3.15 EndZ=0
    g1: LineSegment StartX=36.25 StartY=-3.15 StartZ=0 EndX=38.95 EndY=-3.15 EndZ=0
    g2: LineSegment StartX=41.65 StartY=-3.15 StartZ=0 EndX=41.65 EndY=-7.15 EndZ=0
    g3: LineSegment StartX=38.95 StartY=-7.15 StartZ=0 EndX=41.65 EndY=-7.15 EndZ=0
    g4: LineSegment StartX=38.95 StartY=-7.15 StartZ=0 EndX=36.25 EndY=-7.15 EndZ=0
    g5: LineSegment StartX=36.25 StartY=-3.15 StartZ=0 EndX=36.25 EndY=-7.15 EndZ=0
  constraints (16):
    c: Horizontal(g0)
    c: Distance(g0) = 2.7
    c: Horizontal(g1)
    c: Distance(g1) = 2.7
    c: Coincident(g1,g0)
    c: Block(g0)
    c: Coincident(g2,g0)
    c: Vertical(g2)
    c: Horizontal(g3)
    c: Coincident(g3,g2)
    c: Horizontal(g4)
    c: Coincident(g5,g1)
    c: Vertical(g5)
    c: Coincident(g5,g4)
    c: Block(g3)
    c: Block(g4)
FEATURE [Sketcher::SketchObject] Sketch022
  FullyConstrained = true
  Placement = pos=(0,-14.3,2.37) rot=(-1,0,0;2.03453rad)
  sketch-geometry (6):
    g0: LineSegment StartX=41.65 StartY=-3.15 StartZ=0 EndX=38.95 EndY=-3.15 EndZ=0
    g1: LineSegment StartX=36.25 StartY=-3.15 StartZ=0 EndX=38.95 EndY=-3.15 EndZ=0
    g2: LineSegment StartX=41.65 StartY=-3.15 StartZ=0 EndX=41.65 EndY=-7.15 EndZ=0
    g3: LineSegment StartX=38.95 StartY=-7.15 StartZ=0 EndX=41.65 EndY=-7.15 EndZ=0
    g4: LineSegment StartX=38.95 StartY=-7.15 StartZ=0 EndX=36.25 EndY=-7.15 EndZ=0
    g5: LineSegment StartX=36.25 StartY=-3.15 StartZ=0 EndX=36.25 EndY=-7.15 EndZ=0
  constraints (16):
    c: Horizontal(g0)
    c: Distance(g0) = 2.7
    c: Horizontal(g1)
    c: Distance(g1) = 2.7
    c: Coincident(g1,g0)
    c: Block(g0)
    c: Coincident(g2,g0)
    c: Vertical(g2)
    c: Horizontal(g3)
    c: Coincident(g3,g2)
    c: Horizontal(g4)
    c: Coincident(g5,g1)
    c: Vertical(g5)
    c: Coincident(g5,g4)
    c: Block(g3)
    c: Block(g4)
FEATURE [Sketcher::SketchObject] Sketch024
  FullyConstrained = true
  Placement = pos=(0,-14.3,2.37) rot=(-1,0,0;2.03453rad)
  sketch-geometry (4):
    g0: LineSegment StartX=49.5 StartY=-21.2 StartZ=0 EndX=49.5 EndY=-22.8 EndZ=0
    g1: LineSegment StartX=49.5 StartY=-22.8 StartZ=0 EndX=0.002238 EndY=-22.8 EndZ=0
    g2: LineSegment StartX=0.002238 StartY=-21.2 StartZ=0 EndX=0.002238 EndY=-22.8 EndZ=0
    g3: LineSegment StartX=49.5 StartY=-21.2 StartZ=0 EndX=0.002238 EndY=-21.2 EndZ=0
  constraints (10):
    c: Vertical(g0)
    c: Distance(g0) = 1.6
    c: Coincident(g1,g0)
    c: Horizontal(g1)
    c: Vertical(g2)
    c: Coincident(g2,g1)
    c: Coincident(g3,g0)
    c: Coincident(g3,g2)
    c: Horizontal(g3)
    c: Block(g3)
FEATURE [Sketcher::SketchObject] Sketch025
  FullyConstrained = true
  Placement = pos=(0,-14.3,2.37) rot=(-1,0,0;2.03453rad)
  sketch-geometry (4):
    g0: LineSegment StartX=0 StartY=1.5 StartZ=0 EndX=0 EndY=0 EndZ=0
    g1: LineSegment StartX=0 StartY=1.5 StartZ=0 EndX=5 EndY=1.5 EndZ=0
    g2: LineSegment StartX=5 StartY=1.5 StartZ=0 EndX=5 EndY=0 EndZ=0
    g3: LineSegment StartX=0 StartY=0 StartZ=0 EndX=5 EndY=0 EndZ=0
  constraints (13):
    c: Vertical(g0)
    c: Distance(g0) = 1.5
    c: Horizontal(g1)
    c: Distance(g1) = 5
    c: Coincident(g1,g0)
    c: Vertical(g2)
    c: Distance(g2) = 1.5
    c: Coincident(g2,g1)
    c: Block(g1)
    c: Block(g2)
    c: Block(g0)
    c: Coincident(g3,g0)
    c: Coincident(g3,g2)
FEATURE [Part::Extrusion] Extrude022  label="solenoidDriverBottomLipTopExtrude014"
  Base = -> Sketch025
  Dir = (0,0.894389,-0.447291)
  DirMode = 2
  FaceMakerClass = Part::FaceMakerBullseye
  LengthFwd = -6.5
  LengthRev = 0
  Placement = pos=(0,-15.45,20.3) rot=(1,0,0;1.5708rad)
  Solid = true
  Symmetric = false
FEATURE [Part::Fillet] Fillet013  label="solenoidDriverBottomLipTopFillet006"
  Base = -> Extrude022
  Edges = 1 edges r=1.4: [Edge6]
  Placement = pos=(5,0,0) rot=(0,0,1;0rad)
FEATURE [Sketcher::SketchObject] Sketch026
  FullyConstrained = true
  Placement = pos=(0,-14.3,2.37) rot=(-1,0,0;2.03453rad)
  sketch-geometry (4):
    g0: LineSegment StartX=0 StartY=1.5 StartZ=0 EndX=0 EndY=0 EndZ=0
    g1: LineSegment StartX=0 StartY=1.5 StartZ=0 EndX=5 EndY=1.5 EndZ=0
    g2: LineSegment StartX=5 StartY=1.5 StartZ=0 EndX=5 EndY=0 EndZ=0
    g3: LineSegment StartX=0 StartY=0 StartZ=0 EndX=5 EndY=0 EndZ=0
  constraints (13):
    c: Vertical(g0)
    c: Distance(g0) = 1.5
    c: Horizontal(g1)
    c: Distance(g1) = 5
    c: Coincident(g1,g0)
    c: Vertical(g2)
    c: Distance(g2) = 1.5
    c: Coincident(g2,g1)
    c: Block(g1)
    c: Block(g2)
    c: Block(g0)
    c: Coincident(g3,g0)
    c: Coincident(g3,g2)
FEATURE [Part::Extrusion] Extrude023  label="solenoidDriverBottomLipTopExtrude015"
  Base = -> Sketch026
  Dir = (0,0.894389,-0.447291)
  DirMode = 2
  FaceMakerClass = Part::FaceMakerBullseye
  LengthFwd = -6.5
  LengthRev = 0
  Placement = pos=(5,-14.15,19.65) rot=(1,0,0;1.5708rad)
  Solid = true
  Symmetric = false
FEATURE [Sketcher::SketchObject] Sketch027
  FullyConstrained = true
  Placement = pos=(0,-14.3,2.37) rot=(-1,0,0;2.03453rad)
  sketch-geometry (5):
    g0: LineSegment StartX=45.5 StartY=-21.2 StartZ=0 EndX=49.5 EndY=-21.2 EndZ=0
    g1: LineSegment StartX=49.5 StartY=0 StartZ=0 EndX=49.5 EndY=-21.2 EndZ=0
    g2: LineSegment StartX=49.5 StartY=0 StartZ=0 EndX=49.5 EndY=1.6 EndZ=0
    g3: LineSegment StartX=45.5 StartY=-21.2 StartZ=0 EndX=45.5 EndY=1.6 EndZ=0
    g4: LineSegment StartX=49.5 StartY=1.6 StartZ=0 EndX=45.5 EndY=1.6 EndZ=0
  constraints (14):
    c: Horizontal(g0)
    c: Distance(g0) = 4
    c: Coincident(g1,g0)
    c: Vertical(g1)
    c: Block(g1)
    c: Vertical(g2)
    c: Distance(g2) = 1.6
    c: Block(g2)
    c: Coincident(g3,g0)
    c: Vertical(g3)
    c: Coincident(g4,g2)
    c: Horizontal(g4)
    c: Block(g0)
    c: Coincident(g3,g4)
FEATURE [Part::Extrusion] Extrude024
  Base = -> Sketch027
  Dir = (0,0.894389,-0.447291)
  DirMode = 2
  FaceMakerClass = Part::FaceMakerBullseye
  LengthFwd = 6.34
  LengthRev = 0
  Placement = pos=(0,-5.59,1) rot=(0,0,1;0rad)
  Solid = true
  Symmetric = false
FEATURE [Part::Fillet] Fillet014  label="solenoidDriverSideBarFillet014"
  Base = -> Extrude024
  Edges = 1 edges r=1.4: [Edge14]
  Placement = pos=(0,0.9,-0.45) rot=(0,0,1;0rad)
FEATURE [Part::Revolution] Revolve  label="mainScrewStandRevolve"
  Angle = 360
  Axis = (0,0,1)
  Base = (0,0,0)
  FaceMakerClass = Part::FaceMakerBullseye
  Placement = pos=(121.35,-15.3,0) rot=(0,0,1;0rad)
  Solid = true
  Source = -> Sketch004
  Symmetric = false
FEATURE [Part::Extrusion] Extrude021  label="solenoidDriverTopLipLowerExtrude011"
  Base = -> Sketch024
  Dir = (0,0.894389,-0.447291)
  DirMode = 2
  FaceMakerClass = Part::FaceMakerBullseye
  LengthFwd = 5.05
  LengthRev = 0
  Solid = true
  Symmetric = false
FEATURE [Part::Fillet] Fillet012  label="solenoidDriverTopLipLowerFillet004"
  Base = -> Extrude021
  Edges = 1 edges r=1.2: [Edge7]
  Placement = pos=(0,-0.9,-1.35) rot=(0,0,1;0rad)
FEATURE [Part::Fillet] Fillet003  label="solenoidDriverTopLipLowerFillet003"
  Base = -> Extrude010
  Edges = 1 edges r=1.2: [Edge7]
  Placement = pos=(0,-3,-0.3) rot=(0,0,1;0rad)
FEATURE [Part::Extrusion] Extrude025  label="mainBodyUpperExtrude025"
  Base = -> Sketch001
  Dir = (0,0,1)
  DirMode = 2
  FaceMakerClass = Part::FaceMakerBullseye
  LengthFwd = 20
  LengthRev = 0
  Solid = true
  Symmetric = false
FEATURE [Part::MultiFuse] Fusion  label="solenoidDriverBottomLipFusion"
  Placement = pos=(0,-1.6,0) rot=(0,0,1;0rad)
  Shapes = -> [Fillet005,Fillet013,Extrude023,Extrude013]
FEATURE [Sketcher::SketchObject] Sketch028
  FullyConstrained = true
  Placement = pos=(0,-14.3,2.37) rot=(-1,0,0;2.03453rad)
  sketch-geometry (4):
    g0: LineSegment StartX=0 StartY=1.5 StartZ=0 EndX=0 EndY=0 EndZ=0
    g1: LineSegment StartX=0 StartY=1.5 StartZ=0 EndX=5 EndY=1.5 EndZ=0
    g2: LineSegment StartX=5 StartY=1.5 StartZ=0 EndX=5 EndY=0 EndZ=0
    g3: LineSegment StartX=0 StartY=0 StartZ=0 EndX=5 EndY=0 EndZ=0
  constraints (13):
    c: Vertical(g0)
    c: Distance(g0) = 1.5
    c: Horizontal(g1)
    c: Distance(g1) = 5
    c: Coincident(g1,g0)
    c: Vertical(g2)
    c: Distance(g2) = 1.5
    c: Coincident(g2,g1)
    c: Block(g1)
    c: Block(g2)
    c: Block(g0)
    c: Coincident(g3,g0)
    c: Coincident(g3,g2)
FEATURE [Part::Extrusion] Extrude026  label="solenoidDriverBottomLipTopExtrude016"
  Base = -> Sketch028
  Dir = (0,0.894389,-0.447291)
  DirMode = 2
  FaceMakerClass = Part::FaceMakerBullseye
  LengthFwd = -6.5
  LengthRev = 0
  Placement = pos=(5,-14.15,19.65) rot=(1,0,0;1.5708rad)
  Solid = true
  Symmetric = false
FEATURE [Sketcher::SketchObject] Sketch029
  FullyConstrained = true
  Placement = pos=(0,-14.3,2.37) rot=(-1,0,0;2.03453rad)
  sketch-geometry (4):
    g0: LineSegment StartX=0 StartY=1.5 StartZ=0 EndX=0 EndY=0 EndZ=0
    g1: LineSegment StartX=0 StartY=1.5 StartZ=0 EndX=5 EndY=1.5 EndZ=0
    g2: LineSegment StartX=5 StartY=1.5 StartZ=0 EndX=5 EndY=0 EndZ=0
    g3: LineSegment StartX=0 StartY=0 StartZ=0 EndX=5 EndY=0 EndZ=0
  constraints (13):
    c: Vertical(g0)
    c: Distance(g0) = 1.5
    c: Horizontal(g1)
    c: Distance(g1) = 5
    c: Coincident(g1,g0)
    c: Vertical(g2)
    c: Distance(g2) = 1.5
    c: Coincident(g2,g1)
    c: Block(g1)
    c: Block(g2)
    c: Block(g0)
    c: Coincident(g3,g0)
    c: Coincident(g3,g2)
FEATURE [Part::Extrusion] Extrude027  label="solenoidDriverBottomLipTopExtrude017"
  Base = -> Sketch029
  Dir = (0,0.894389,-0.447291)
  DirMode = 2
  FaceMakerClass = Part::FaceMakerBullseye
  LengthFwd = -6.5
  LengthRev = 0
  Placement = pos=(0,-14.15,19.65) rot=(1,0,0;1.5708rad)
  Solid = true
  Symmetric = false
FEATURE [Sketcher::SketchObject] Sketch030
  FullyConstrained = true
  Placement = pos=(0,-14.3,2.37) rot=(-1,0,0;2.03453rad)
  sketch-geometry (4):
    g0: LineSegment StartX=0 StartY=1.5 StartZ=0 EndX=0 EndY=0 EndZ=0
    g1: LineSegment StartX=0 StartY=1.5 StartZ=0 EndX=5 EndY=1.5 EndZ=0
    g2: LineSegment StartX=5 StartY=1.5 StartZ=0 EndX=5 EndY=0 EndZ=0
    g3: LineSegment StartX=0 StartY=0 StartZ=0 EndX=5 EndY=0 EndZ=0
  constraints (13):
    c: Vertical(g0)
    c: Distance(g0) = 1.5
    c: Horizontal(g1)
    c: Distance(g1) = 5
    c: Coincident(g1,g0)
    c: Vertical(g2)
    c: Distance(g2) = 1.5
    c: Coincident(g2,g1)
    c: Block(g1)
    c: Block(g2)
    c: Block(g0)
    c: Coincident(g3,g0)
    c: Coincident(g3,g2)
FEATURE [Sketcher::SketchObject] Sketch031
  FullyConstrained = true
  Placement = pos=(0,-14.3,2.37) rot=(-1,0,0;2.03453rad)
  sketch-geometry (6):
    g0: LineSegment StartX=45.5 StartY=-21.2 StartZ=0 EndX=49.5 EndY=-21.2 EndZ=0
    g1: LineSegment StartX=45.5 StartY=0 StartZ=0 EndX=49.5 EndY=0 EndZ=0
    g2: LineSegment StartX=49.5 StartY=0 StartZ=0 EndX=49.5 EndY=-21.2 EndZ=0
    g3: LineSegment StartX=4 StartY=0 StartZ=0 EndX=4 EndY=-21.2 EndZ=0
    g4: LineSegment StartX=45.5 StartY=-21.2 StartZ=0 EndX=4 EndY=-21.2 EndZ=0
    g5: LineSegment StartX=4 StartY=0 StartZ=0 EndX=45.5 EndY=0 EndZ=0
  constraints (16):
    c: Horizontal(g0)
    c: Distance(g0) = 4
    c: Horizontal(g1)
    c: Distance(g1) = 4
    c: Coincident(g2,g1)
    c: Coincident(g2,g0)
    c: Vertical(g2)
    c: Block(g2)
    c: Vertical(g3)
    c: Coincident(g4,g0)
    c: Horizontal(g4)
    c: Coincident(g4,g3)
    c: Coincident(g5,g1)
    c: Horizontal(g5)
    c: Block(g3)
    c: Block(g5)
FEATURE [Part::Extrusion] Extrude028  label="removeFromSolenoidDriverMainExtrude021"
  Base = -> Sketch031
  Dir = (0,0.894389,-0.447291)
  DirMode = 2
  FaceMakerClass = Part::FaceMakerBullseye
  LengthFwd = 3.1
  LengthRev = 0
  Placement = pos=(-4,-2.42,-0.8) rot=(0,0,1;0rad)
  Solid = true
  Symmetric = false
FEATURE [Part::Extrusion] Extrude029  label="solenoidDriverBottomLipTopExtrude018"
  Base = -> Sketch030
  Dir = (0,0.894389,-0.447291)
  DirMode = 2
  FaceMakerClass = Part::FaceMakerBullseye
  LengthFwd = -6.5
  LengthRev = 0
  Placement = pos=(5,-14.15,19.65) rot=(1,0,0;1.5708rad)
  Solid = true
  Symmetric = false
FEATURE [Sketcher::SketchObject] Sketch032
  FullyConstrained = true
  Placement = pos=(0,-14.3,2.37) rot=(-1,0,0;2.03453rad)
  sketch-geometry (4):
    g0: LineSegment StartX=0 StartY=1.5 StartZ=0 EndX=0 EndY=0 EndZ=0
    g1: LineSegment StartX=0 StartY=1.5 StartZ=0 EndX=5 EndY=1.5 EndZ=0
    g2: LineSegment StartX=5 StartY=1.5 StartZ=0 EndX=5 EndY=0 EndZ=0
    g3: LineSegment StartX=0 StartY=0 StartZ=0 EndX=5 EndY=0 EndZ=0
  constraints (13):
    c: Vertical(g0)
    c: Distance(g0) = 1.5
    c: Horizontal(g1)
    c: Distance(g1) = 5
    c: Coincident(g1,g0)
    c: Vertical(g2)
    c: Distance(g2) = 1.5
    c: Coincident(g2,g1)
    c: Block(g1)
    c: Block(g2)
    c: Block(g0)
    c: Coincident(g3,g0)
    c: Coincident(g3,g2)
FEATURE [Part::Extrusion] Extrude030  label="solenoidDriverBottomLipTopExtrude019"
  Base = -> Sketch032
  Dir = (0,0.894389,-0.447291)
  DirMode = 2
  FaceMakerClass = Part::FaceMakerBullseye
  LengthFwd = -6.5
  LengthRev = 0
  Placement = pos=(0,-14.15,19.65) rot=(1,0,0;1.5708rad)
  Solid = true
  Symmetric = false
FEATURE [Part::MultiFuse] Fusion004
  Placement = pos=(0,1.4,2.65) rot=(0,0,1;0rad)
  Shapes = -> [Extrude029,Extrude030]
FEATURE [Part::MultiFuse] Fusion003
  Placement = pos=(-2.3,0,0) rot=(0,0,1;0rad)
  Shapes = -> [Extrude028,Fusion004]
FEATURE [Sketcher::SketchObject] Sketch033
  FullyConstrained = true
  Placement = pos=(0,-14.3,2.37) rot=(-1,0,0;2.03453rad)
  sketch-geometry (4):
    g0: LineSegment StartX=0 StartY=1.5 StartZ=0 EndX=0 EndY=0 EndZ=0
    g1: LineSegment StartX=0 StartY=1.5 StartZ=0 EndX=5 EndY=1.5 EndZ=0
    g2: LineSegment StartX=5 StartY=1.5 StartZ=0 EndX=5 EndY=0 EndZ=0
    g3: LineSegment StartX=0 StartY=0 StartZ=0 EndX=5 EndY=0 EndZ=0
  constraints (13):
    c: Vertical(g0)
    c: Distance(g0) = 1.5
    c: Horizontal(g1)
    c: Distance(g1) = 5
    c: Coincident(g1,g0)
    c: Vertical(g2)
    c: Distance(g2) = 1.5
    c: Coincident(g2,g1)
    c: Block(g1)
    c: Block(g2)
    c: Block(g0)
    c: Coincident(g3,g0)
    c: Coincident(g3,g2)
FEATURE [Sketcher::SketchObject] Sketch034
  FullyConstrained = true
  Placement = pos=(0,-14.3,2.37) rot=(-1,0,0;2.03453rad)
  sketch-geometry (4):
    g0: LineSegment StartX=0 StartY=1.5 StartZ=0 EndX=0 EndY=0 EndZ=0
    g1: LineSegment StartX=0 StartY=1.5 StartZ=0 EndX=5 EndY=1.5 EndZ=0
    g2: LineSegment StartX=5 StartY=1.5 StartZ=0 EndX=5 EndY=0 EndZ=0
    g3: LineSegment StartX=0 StartY=0 StartZ=0 EndX=5 EndY=0 EndZ=0
  constraints (13):
    c: Vertical(g0)
    c: Distance(g0) = 1.5
    c: Horizontal(g1)
    c: Distance(g1) = 5
    c: Coincident(g1,g0)
    c: Vertical(g2)
    c: Distance(g2) = 1.5
    c: Coincident(g2,g1)
    c: Block(g1)
    c: Block(g2)
    c: Block(g0)
    c: Coincident(g3,g0)
    c: Coincident(g3,g2)
FEATURE [Part::Extrusion] Extrude020  label="removeFromSolenoidDriverMainExtrude020"
  Base = -> Sketch020
  Dir = (0,0.894389,-0.447291)
  DirMode = 2
  FaceMakerClass = Part::FaceMakerBullseye
  LengthFwd = 3.1
  LengthRev = 0
  Placement = pos=(-4,-2.42,-0.8) rot=(0,0,1;0rad)
  Solid = true
  Symmetric = false
FEATURE [Part::Fillet] Fillet
  Base = -> Fusion003
  Edges = 1 edges r=10: [Edge5]
  Placement = pos=(-2,0,0) rot=(0,0,1;0rad)
FEATURE [Part::MultiFuse] Fusion001
  Placement = pos=(0,1.4,2.65) rot=(0,0,1;0rad)
  Shapes = -> [Extrude026,Extrude027]
FEATURE [Part::MultiFuse] Fusion002
  Shapes = -> [Extrude020,Fusion001]
FEATURE [Sketcher::SketchObject] Sketch035
  FullyConstrained = true
  Placement = pos=(0,-14.3,2.37) rot=(-1,0,0;2.03453rad)
  sketch-geometry (4):
    g0: LineSegment StartX=0 StartY=1.5 StartZ=0 EndX=0 EndY=0 EndZ=0
    g1: LineSegment StartX=0 StartY=1.5 StartZ=0 EndX=5 EndY=1.5 EndZ=0
    g2: LineSegment StartX=5 StartY=1.5 StartZ=0 EndX=5 EndY=0 EndZ=0
    g3: LineSegment StartX=0 StartY=0 StartZ=0 EndX=5 EndY=0 EndZ=0
  constraints (13):
    c: Vertical(g0)
    c: Distance(g0) = 1.5
    c: Horizontal(g1)
    c: Distance(g1) = 5
    c: Coincident(g1,g0)
    c: Vertical(g2)
    c: Distance(g2) = 1.5
    c: Coincident(g2,g1)
    c: Block(g1)
    c: Block(g2)
    c: Block(g0)
    c: Coincident(g3,g0)
    c: Coincident(g3,g2)
FEATURE [Sketcher::SketchObject] Sketch036
  FullyConstrained = true
  Placement = pos=(0,-14.3,2.37) rot=(-1,0,0;2.03453rad)
  sketch-geometry (4):
    g0: LineSegment StartX=0 StartY=1.5 StartZ=0 EndX=0 EndY=0 EndZ=0
    g1: LineSegment StartX=0 StartY=1.5 StartZ=0 EndX=5 EndY=1.5 EndZ=0
    g2: LineSegment StartX=5 StartY=1.5 StartZ=0 EndX=5 EndY=0 EndZ=0
    g3: LineSegment StartX=0 StartY=0 StartZ=0 EndX=5 EndY=0 EndZ=0
  constraints (13):
    c: Vertical(g0)
    c: Distance(g0) = 1.5
    c: Horizontal(g1)
    c: Distance(g1) = 5
    c: Coincident(g1,g0)
    c: Vertical(g2)
    c: Distance(g2) = 1.5
    c: Coincident(g2,g1)
    c: Block(g1)
    c: Block(g2)
    c: Block(g0)
    c: Coincident(g3,g0)
    c: Coincident(g3,g2)
FEATURE [Part::Extrusion] Extrude031  label="solenoidDriverBottomLipTopExtrude020"
  Base = -> Sketch035
  Dir = (0,0.894389,-0.447291)
  DirMode = 2
  FaceMakerClass = Part::FaceMakerBullseye
  LengthFwd = -6.5
  LengthRev = 0
  Placement = pos=(5,-14.15,19.65) rot=(1,0,0;1.5708rad)
  Solid = true
  Symmetric = false
FEATURE [Part::Extrusion] Extrude032  label="solenoidDriverBottomLipTopExtrude021"
  Base = -> Sketch036
  Dir = (0,0.894389,-0.447291)
  DirMode = 2
  FaceMakerClass = Part::FaceMakerBullseye
  LengthFwd = -6.5
  LengthRev = 0
  Placement = pos=(0,-14.15,19.65) rot=(1,0,0;1.5708rad)
  Solid = true
  Symmetric = false
FEATURE [Part::MultiFuse] Fusion009
  Placement = pos=(8,1.4,2.65) rot=(0,0,1;0rad)
  Shapes = -> [Extrude031,Extrude032]
FEATURE [Part::MultiFuse] Fusion010  label="removeFromSolenoidDriver"
  Shapes = -> [Fusion009,Fillet,Fusion002]
FEATURE [Sketcher::SketchObject] Sketch037
  FullyConstrained = true
  Placement = pos=(0,0,0) rot=(1,0,0;1.5708rad)
  sketch-geometry (4):
    g0: Circle CenterX=64.05 CenterY=16.5 CenterZ=0 NormalX=0 NormalY=0 NormalZ=1 AngleXU=0 Radius=2.7
    g1: Circle CenterX=64.05 CenterY=8.5 CenterZ=0 NormalX=0 NormalY=0 NormalZ=1 AngleXU=0 Radius=2.7
    g2: Circle CenterX=84.15 CenterY=8.5 CenterZ=0 NormalX=0 NormalY=0 NormalZ=1 AngleXU=0 Radius=2.7
    g3: Circle CenterX=84.15 CenterY=16.5 CenterZ=0 NormalX=0 NormalY=0 NormalZ=1 AngleXU=0 Radius=2.7
  constraints (4):
    c: Block(g2)
    c: Block(g3)
    c: Block(g0)
    c: Block(g1)
FEATURE [Part::Extrusion] Extrude033  label="removeFromMainBodyToCreateScrewHoleCounterSinks001"
  Base = -> Sketch037
  Dir = (0,-1,1.1e-15)
  DirMode = 2
  FaceMakerClass = Part::FaceMakerBullseye
  LengthFwd = 1.9
  LengthRev = 0
  Placement = pos=(0.8,0,0) rot=(0,0,1;0rad)
  Solid = true
  Symmetric = false
FEATURE [Part::MultiFuse] Fusion011  label="removeFromMainBodyToCreateScrewHoleCounterSinks001Fusion011"
  Shapes = -> [Extrude014,Extrude033]
FEATURE [Sketcher::SketchObject] Sketch038
  FullyConstrained = true
  Placement = pos=(0,-14.3,2.37) rot=(-1,0,0;2.03453rad)
  sketch-geometry (4):
    g0: LineSegment StartX=33.9 StartY=-9.7 StartZ=0 EndX=33.9 EndY=-1.5 EndZ=0
    g1: LineSegment StartX=33.9 StartY=-1.5 StartZ=0 EndX=44.5 EndY=-1.5 EndZ=0
    g2: LineSegment StartX=33.9 StartY=-9.7 StartZ=0 EndX=44.5 EndY=-9.7 EndZ=0
    g3: LineSegment StartX=44.5 StartY=-1.5 StartZ=0 EndX=44.5 EndY=-9.7 EndZ=0
  constraints (10):
    c: Vertical(g0)
    c: Coincident(g1,g0)
    c: Horizontal(g1)
    c: Block(g1)
    c: Block(g0)
    c: Coincident(g2,g0)
    c: Horizontal(g2)
    c: Coincident(g3,g1)
    c: Coincident(g3,g2)
    c: Vertical(g3)
FEATURE [Part::Extrusion] Extrude034
  Base = -> Sketch038
  Dir = (0,0.894389,-0.447291)
  DirMode = 2
  FaceMakerClass = Part::FaceMakerBullseye
  LengthFwd = 16
  LengthRev = 0
  Placement = pos=(0,-22,7) rot=(0,0,1;0rad)
  Solid = true
  Symmetric = false
FEATURE [Sketcher::SketchObject] Sketch039
  FullyConstrained = true
  Placement = pos=(0,-14.3,2.37) rot=(-1,0,0;2.03453rad)
  sketch-geometry (4):
    g0: LineSegment StartX=5.5 StartY=-7.7 StartZ=0 EndX=13.3 EndY=-7.7 EndZ=0
    g1: LineSegment StartX=13.3 StartY=-7.7 StartZ=0 EndX=13.3 EndY=-13.1 EndZ=0
    g2: LineSegment StartX=13.3 StartY=-13.1 StartZ=0 EndX=5.5 EndY=-13.1 EndZ=0
    g3: LineSegment StartX=5.5 StartY=-7.7 StartZ=0 EndX=5.5 EndY=-13.1 EndZ=0
  constraints (12):
    c: Horizontal(g0)
    c: Distance(g0) = 7.8
    c: Coincident(g1,g0)
    c: Vertical(g1)
    c: Distance(g1) = 5.4
    c: Coincident(g2,g1)
    c: Horizontal(g2)
    c: Vertical(g3)
    c: Coincident(g3,g2)
    c: Block(g0)
    c: Block(g2)
    c: Block(g3)
FEATURE [Part::Extrusion] Extrude035  label="removeToMakeHoleForConnectorExtrude035"
  Base = -> Sketch039
  Dir = (0,0.894389,-0.447291)
  DirMode = 2
  FaceMakerClass = Part::FaceMakerBullseye
  LengthFwd = 15
  LengthRev = 0
  Placement = pos=(-4,-22,9.6469) rot=(0,0,1;0rad)
  Solid = true
  Symmetric = false
FEATURE [App::MeasureDistance] Distance  label="Distance: 4.00 mm"
  Distance = 4.00184
  P1 = (119.349,-15.3,8)
  P2 = (123.351,-15.3,8)
FEATURE [App::MeasureDistance] Distance001  label="Distance: 3.80 mm"
  Distance = 3.8
  P1 = (119.45,-15.3,8)
  P2 = (123.25,-15.3,8)
FEATURE [Part::Fillet] Fillet015
  Base = -> Extrude009
  Edges = 1 edges r=1.59: [Edge7]
FEATURE [Part::Fillet] Fillet016
  Base = -> Extrude017
  Edges = 1 edges r=1.49: [Edge12]
FEATURE [Part::Fillet] Fillet017
  Base = -> Fillet016
  Edges = 1 edges r=1.45: [Edge8]
FEATURE [Part::MultiFuse] Fusion012  label="main"
  Shapes = -> [Extrude,Revolve,Extrude005,Fillet003,Fillet012,Fillet014,Extrude025,Fusion,Fillet015,Fillet017]
FEATURE [Part::Cut] Cut001
  Base = -> Fusion012
  Tool = -> Box003
FEATURE [Part::Cut] Cut002
  Base = -> Cut001
  Tool = -> Box002
FEATURE [Part::Cut] Cut003
  Base = -> Cut002
  Tool = -> Cut
FEATURE [Part::Cut] Cut004
  Base = -> Cut003
  Tool = -> Extrude019
FEATURE [Part::Cut] Cut005
  Base = -> Cut004
  Tool = -> Fusion011
FEATURE [Part::Cut] Cut006
  Base = -> Cut005
  Tool = -> Extrude004
FEATURE [Part::Cut] Cut007
  Base = -> Cut006
  Tool = -> Extrude015
FEATURE [Part::Cut] Cut008
  Base = -> Cut007
  Tool = -> Extrude008
FEATURE [Part::Cut] Cut009
  Base = -> Cut008
  Tool = -> Fusion010
FEATURE [App::MeasureDistance] Distance002  label="Distance: 2.05 mm"
  Distance = 2.05453
  P1 = (1.5,-23.0732,21.402)
  P2 = (6e-15,-23,20)
FEATURE [Part::Cut] Cut010
  Base = -> Cut009
  Tool = -> Extrude035
FEATURE [Part::Cut] Cut011
  Base = -> Cut010
  Tool = -> Extrude034
FEATURE [Part::Fillet] Fillet018
  Base = -> Cut011
  Edges = 1 edges r=3: [Edge134]
FEATURE [Part::Fillet] Fillet019
  Base = -> Fillet018
  Edges = 1 edges r=3: [Edge29]
FEATURE [Part::Box] Box004  label="Cube004"
  AttacherType = Attacher::AttachEngine3D
  Height = 10
  Length = 200
  Placement = pos=(-30,0,0) rot=(0,0,1;0rad)
  Width = 10
FEATURE [Part::Fillet] Fillet020
  Base = -> Box004
  Edges = 1 edges r=3.6: [Edge12]
FEATURE [Part::Box] Box005  label="Cube005"
  AttacherType = Attacher::AttachEngine3D
  Height = 10
  Length = 198
  Placement = pos=(-30,0,0) rot=(0,0,1;0rad)
  Width = 10
FEATURE [Part::Cut] Cut012
  Base = -> Box005
  Tool = -> Fillet020
FEATURE [Part::Box] Box006  label="Cube006"
  AttacherType = Attacher::AttachEngine3D
  Height = 5
  Length = 200
  Placement = pos=(-30,6.4,10) rot=(1,0,0;0rad)
  Width = 5
FEATURE [Part::Box] Box007  label="Cube007"
  AttacherType = Attacher::AttachEngine3D
  Height = 5
  Length = 200
  Placement = pos=(-30,6.4,10) rot=(1,0,0;0.872665rad)
  Width = 5
FEATURE [Part::MultiFuse] Fusion013  label="removeFromMainFusion013"
  Placement = pos=(0,-10,10) rot=(0,0,1;0rad)
  Shapes = -> [Box007,Box006,Cut012]
FEATURE [Part::Cut] Cut013
  Base = -> Fillet019
  Tool = -> Fusion013
FEATURE [Mesh::Feature] v0_98_Cut013  label="v0_98-Cut013"
FEATURE [App::MeasureDistance] Distance003  label="Distance: 7.18 mm"
  Distance = 7.17719
  P1 = (117.773,-15.3145,-2.4)
  P2 = (124.951,-15.2973,-2.4)
